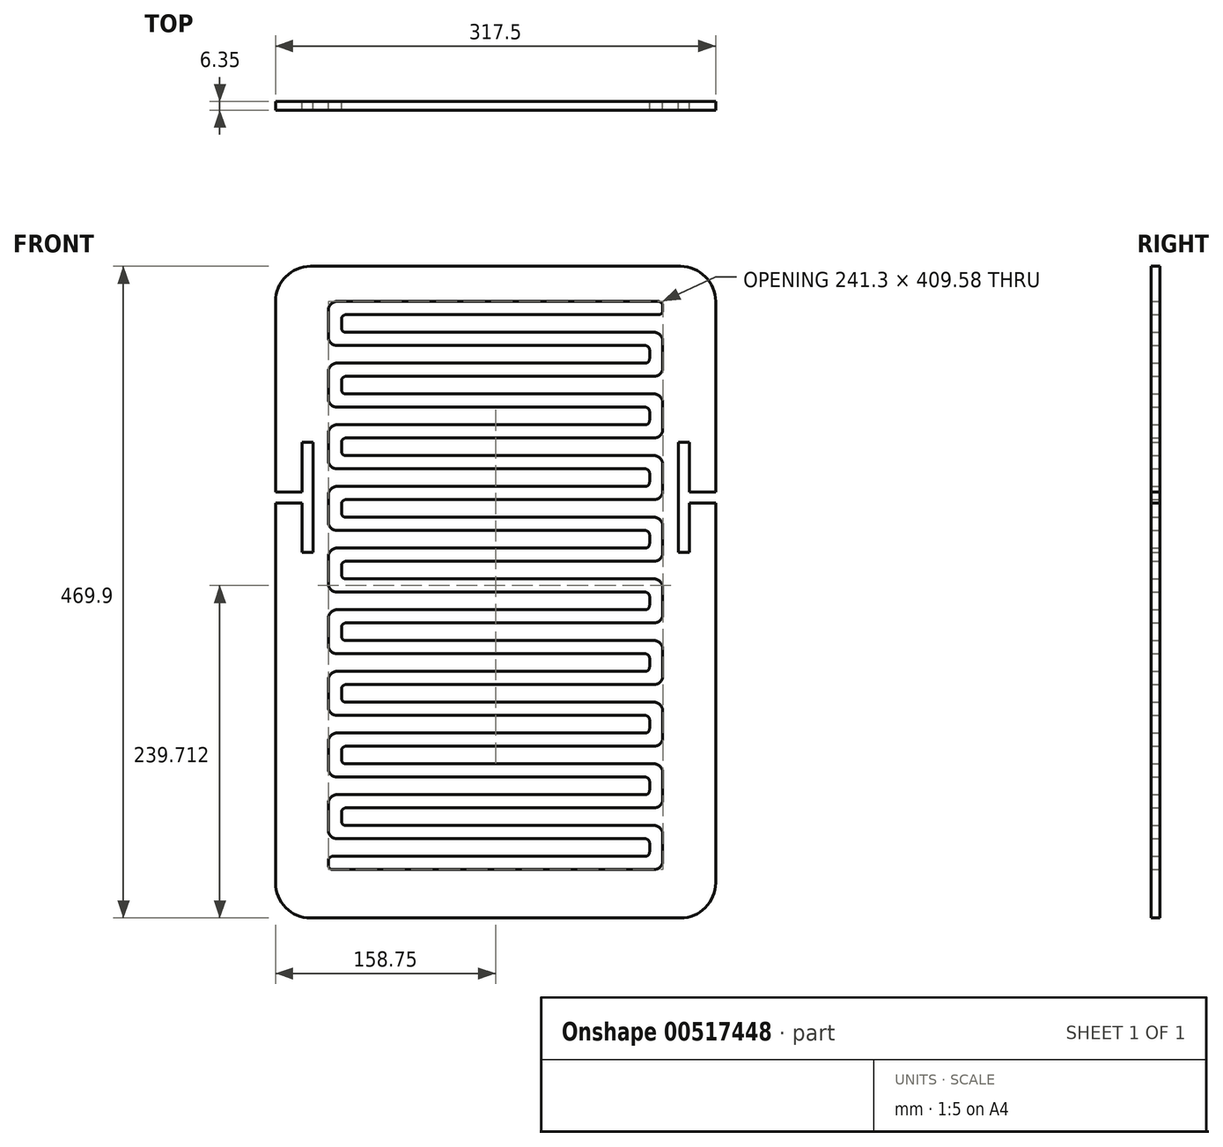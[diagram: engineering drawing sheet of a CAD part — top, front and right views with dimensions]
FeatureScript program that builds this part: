
annotation { "Feature Type Name" : "Feature", "Feature Type Description" : "" }
export const myFeature = defineFeature(function(context is Context, id is Id, definition is map)
    precondition{}
    {
        {
            var Q0;
            Q0=qCreatedBy(makeId("Front.planeOp"),FACE);
            var sketch = newSketch(context, id + "F0", { "sketchPlane" : qUnion([Q0])});
            skLineSegment(sketch, "E0.bottom", {"start": v(133.35, -234.95) * mm, "end": v(-133.35, -234.95) * mm});
            skLineSegment(sketch, "E0.top", {"start": v(133.35, 234.95) * mm, "end": v(-133.35, 234.95) * mm});
            skLineSegment(sketch, "E0.left", {"start": v(158.75, -209.55) * mm, "end": v(158.75, 209.55) * mm});
            skLineSegment(sketch, "E0.right", {"start": v(-158.75, -209.55) * mm, "end": v(-158.75, 209.55) * mm});
            skPoint(sketch, "E0.middle", {"position": v(0, 0) * mm});
            skPoint(sketch, "E1.visualSharp", {"position": v(-158.75, 234.95) * mm});
            skArc(sketch, "E1.filletArc", {"start": v(-133.35, 234.95) * mm, "mid": v(-151.31, 227.51) * mm, "end": v(-158.75, 209.55) * mm});
            skPoint(sketch, "E2.visualSharp", {"position": v(158.75, 234.95) * mm});
            skArc(sketch, "E2.filletArc", {"start": v(158.75, 209.55) * mm, "mid": v(151.31, 227.51) * mm, "end": v(133.35, 234.95) * mm});
            skPoint(sketch, "E3.visualSharp", {"position": v(158.75, -234.95) * mm});
            skArc(sketch, "E3.filletArc", {"start": v(133.35, -234.95) * mm, "mid": v(151.31, -227.51) * mm, "end": v(158.75, -209.55) * mm});
            skPoint(sketch, "E4.visualSharp", {"position": v(-158.75, -234.95) * mm});
            skArc(sketch, "E4.filletArc", {"start": v(-158.75, -209.55) * mm, "mid": v(-151.31, -227.51) * mm, "end": v(-133.35, -234.95) * mm});
            skLineSegment(sketch, "E5.bottom", {"start": v(-139.7, 107.95) * mm, "end": v(-131.76, 107.95) * mm});
            skLineSegment(sketch, "E5.top", {"start": v(-139.7, 28.58) * mm, "end": v(-131.76, 28.58) * mm});
            skLineSegment(sketch, "E5.left", {"start": v(-139.7, 107.95) * mm, "end": v(-139.7, 28.58) * mm});
            skLineSegment(sketch, "E5.right", {"start": v(-131.76, 107.95) * mm, "end": v(-131.76, 28.58) * mm});
            skLineSegment(sketch, "E6.MirrorCS", {"start": v(139.7, 107.95) * mm, "end": v(131.76, 107.95) * mm});
            skLineSegment(sketch, "E7.MirrorCS", {"start": v(139.7, 28.58) * mm, "end": v(131.76, 28.58) * mm});
            skLineSegment(sketch, "E8.MirrorCS", {"start": v(131.76, 107.95) * mm, "end": v(131.76, 28.58) * mm});
            skLineSegment(sketch, "E9.MirrorCS", {"start": v(139.7, 107.95) * mm, "end": v(139.7, 28.58) * mm});
            skLineSegment(sketch, "E10", {"start": v(-114.3, 209.55) * mm, "end": v(117.47, 209.55) * mm});
            skLineSegment(sketch, "E11", {"start": v(120.65, 206.38) * mm, "end": v(120.65, 203.2) * mm});
            skLineSegment(sketch, "E12", {"start": v(117.47, 200.03) * mm, "end": v(-107.95, 200.03) * mm});
            skLineSegment(sketch, "E13", {"start": v(-111.13, 196.85) * mm, "end": v(-111.13, 190.5) * mm});
            skLineSegment(sketch, "E14", {"start": v(-107.95, 187.33) * mm, "end": v(114.3, 187.33) * mm});
            skLineSegment(sketch, "E15", {"start": v(120.65, 180.97) * mm, "end": v(120.65, 161.93) * mm});
            skLineSegment(sketch, "E16", {"start": v(-120.65, 203.2) * mm, "end": v(-120.65, 184.15) * mm});
            skLineSegment(sketch, "E17", {"start": v(-114.3, 177.8) * mm, "end": v(107.95, 177.8) * mm});
            skLineSegment(sketch, "E18", {"start": v(111.12, 174.62) * mm, "end": v(111.12, 168.28) * mm});
            skLineSegment(sketch, "E19", {"start": v(107.95, 165.1) * mm, "end": v(-114.3, 165.1) * mm});
            skPoint(sketch, "E20.visualSharp", {"position": v(-120.65, 209.55) * mm});
            skArc(sketch, "E20.filletArc", {"start": v(-114.3, 209.55) * mm, "mid": v(-118.8, 207.7) * mm, "end": v(-120.65, 203.2) * mm});
            skPoint(sketch, "E21.visualSharp", {"position": v(-111.13, 200.03) * mm});
            skArc(sketch, "E21.filletArc", {"start": v(-107.95, 200.03) * mm, "mid": v(-110.2, 199.1) * mm, "end": v(-111.13, 196.85) * mm});
            skPoint(sketch, "E22.visualSharp", {"position": v(-111.13, 187.33) * mm});
            skArc(sketch, "E22.filletArc", {"start": v(-111.13, 190.5) * mm, "mid": v(-110.2, 188.25) * mm, "end": v(-107.95, 187.33) * mm});
            skPoint(sketch, "E23.visualSharp", {"position": v(-120.65, 177.8) * mm});
            skArc(sketch, "E23.filletArc", {"start": v(-120.65, 184.15) * mm, "mid": v(-118.8, 179.66) * mm, "end": v(-114.3, 177.8) * mm});
            skPoint(sketch, "E24.visualSharp", {"position": v(120.65, 187.33) * mm});
            skArc(sketch, "E24.filletArc", {"start": v(120.65, 180.97) * mm, "mid": v(118.8, 185.47) * mm, "end": v(114.3, 187.32) * mm});
            skPoint(sketch, "E25.visualSharp", {"position": v(120.65, 200.03) * mm});
            skArc(sketch, "E25.filletArc", {"start": v(117.47, 200.03) * mm, "mid": v(119.72, 200.95) * mm, "end": v(120.65, 203.2) * mm});
            skPoint(sketch, "E26.visualSharp", {"position": v(120.65, 209.55) * mm});
            skArc(sketch, "E26.filletArc", {"start": v(120.65, 206.38) * mm, "mid": v(119.72, 208.62) * mm, "end": v(117.47, 209.55) * mm});
            skPoint(sketch, "E27.visualSharp", {"position": v(111.12, 177.8) * mm});
            skArc(sketch, "E27.filletArc", {"start": v(111.12, 174.62) * mm, "mid": v(110.2, 176.87) * mm, "end": v(107.95, 177.8) * mm});
            skPoint(sketch, "E28.visualSharp", {"position": v(111.12, 165.1) * mm});
            skArc(sketch, "E28.filletArc", {"start": v(107.95, 165.1) * mm, "mid": v(110.2, 166.03) * mm, "end": v(111.12, 168.28) * mm});
            skArc(sketch, "E29.filletArc", {"start": v(114.3, 155.58) * mm, "mid": v(118.8, 157.43) * mm, "end": v(120.65, 161.93) * mm});
            skPoint(sketch, "E30.visualSharp", {"position": v(-120.65, 165.1) * mm});
            skLineSegment(sketch, "E31", {"start": v(114.3, 155.58) * mm, "end": v(-107.95, 155.58) * mm});
            skLineSegment(sketch, "E32.0.1.0", {"start": v(114.3, 111.13) * mm, "end": v(-107.95, 111.13) * mm});
            skLineSegment(sketch, "E32.0.1.1", {"start": v(107.95, 120.65) * mm, "end": v(-114.3, 120.65) * mm});
            skArc(sketch, "E32.0.1.2", {"start": v(114.3, 111.13) * mm, "mid": v(118.8, 112.98) * mm, "end": v(120.65, 117.48) * mm});
            skLineSegment(sketch, "E32.0.1.3", {"start": v(120.65, 136.53) * mm, "end": v(120.65, 117.48) * mm});
            skArc(sketch, "E32.0.1.4", {"start": v(107.95, 120.65) * mm, "mid": v(110.2, 121.58) * mm, "end": v(111.12, 123.83) * mm});
            skLineSegment(sketch, "E32.0.1.5", {"start": v(111.13, 130.18) * mm, "end": v(111.13, 123.83) * mm});
            skArc(sketch, "E32.0.1.6", {"start": v(111.12, 130.18) * mm, "mid": v(110.2, 132.42) * mm, "end": v(107.95, 133.35) * mm});
            skArc(sketch, "E32.0.1.7", {"start": v(120.65, 136.53) * mm, "mid": v(118.8, 141.02) * mm, "end": v(114.3, 142.88) * mm});
            skLineSegment(sketch, "E32.0.1.8", {"start": v(-107.95, 142.88) * mm, "end": v(114.3, 142.88) * mm});
            skLineSegment(sketch, "E32.0.1.9", {"start": v(-114.3, 133.35) * mm, "end": v(107.95, 133.35) * mm});
            skArc(sketch, "E32.0.1.10", {"start": v(-120.65, 139.7) * mm, "mid": v(-118.8, 135.2) * mm, "end": v(-114.3, 133.35) * mm});
            skLineSegment(sketch, "E32.0.1.11", {"start": v(-120.65, 158.75) * mm, "end": v(-120.65, 139.7) * mm});
            skArc(sketch, "E32.0.1.12", {"start": v(-114.3, 165.1) * mm, "mid": v(-118.8, 163.24) * mm, "end": v(-120.65, 158.75) * mm});
            skArc(sketch, "E32.0.1.13", {"start": v(-107.95, 155.58) * mm, "mid": v(-110.2, 154.65) * mm, "end": v(-111.13, 152.4) * mm});
            skLineSegment(sketch, "E32.0.1.14", {"start": v(-111.12, 152.4) * mm, "end": v(-111.12, 146.05) * mm});
            skArc(sketch, "E32.0.1.15", {"start": v(-111.13, 146.05) * mm, "mid": v(-110.2, 143.8) * mm, "end": v(-107.95, 142.88) * mm});
            skLineSegment(sketch, "E32.direction1", {"start": v(-107.95, 155.58) * mm, "end": v(-82.55, 155.58) * mm, "construction": true});
            skLineSegment(sketch, "E32.direction2", {"start": v(-107.95, 155.58) * mm, "end": v(-107.95, 111.13) * mm, "construction": true});
            skLineSegment(sketch, "E33.0.0.2", {"start": v(114.3, 66.68) * mm, "end": v(-107.95, 66.68) * mm});
            skLineSegment(sketch, "E33.3.0.2", {"start": v(107.95, 76.2) * mm, "end": v(-114.3, 76.2) * mm});
            skArc(sketch, "E33.6.0.2", {"start": v(114.3, 66.68) * mm, "mid": v(118.8, 68.53) * mm, "end": v(120.65, 73.03) * mm});
            skLineSegment(sketch, "E33.10.0.2", {"start": v(120.65, 92.08) * mm, "end": v(120.65, 73.03) * mm});
            skArc(sketch, "E33.13.0.2", {"start": v(107.95, 76.2) * mm, "mid": v(110.2, 77.13) * mm, "end": v(111.12, 79.38) * mm});
            skLineSegment(sketch, "E33.17.0.2", {"start": v(111.13, 85.73) * mm, "end": v(111.13, 79.38) * mm});
            skArc(sketch, "E33.20.0.2", {"start": v(111.12, 85.73) * mm, "mid": v(110.2, 87.97) * mm, "end": v(107.95, 88.9) * mm});
            skArc(sketch, "E33.24.0.2", {"start": v(120.65, 92.08) * mm, "mid": v(118.8, 96.57) * mm, "end": v(114.3, 98.43) * mm});
            skLineSegment(sketch, "E33.28.0.2", {"start": v(-107.95, 98.43) * mm, "end": v(114.3, 98.43) * mm});
            skLineSegment(sketch, "E33.31.0.2", {"start": v(-114.3, 88.9) * mm, "end": v(107.95, 88.9) * mm});
            skArc(sketch, "E33.34.0.2", {"start": v(-120.65, 95.25) * mm, "mid": v(-118.8, 90.76) * mm, "end": v(-114.3, 88.9) * mm});
            skLineSegment(sketch, "E33.38.0.2", {"start": v(-120.65, 114.3) * mm, "end": v(-120.65, 95.25) * mm});
            skArc(sketch, "E33.41.0.2", {"start": v(-114.3, 120.65) * mm, "mid": v(-118.8, 118.8) * mm, "end": v(-120.65, 114.3) * mm});
            skArc(sketch, "E33.45.0.2", {"start": v(-107.95, 111.13) * mm, "mid": v(-110.2, 110.2) * mm, "end": v(-111.13, 107.95) * mm});
            skLineSegment(sketch, "E33.49.0.2", {"start": v(-111.12, 107.95) * mm, "end": v(-111.12, 101.6) * mm});
            skArc(sketch, "E33.52.0.2", {"start": v(-111.13, 101.6) * mm, "mid": v(-110.2, 99.35) * mm, "end": v(-107.95, 98.43) * mm});
            skLineSegment(sketch, "E33.0.0.3", {"start": v(114.3, 22.23) * mm, "end": v(-107.95, 22.23) * mm});
            skLineSegment(sketch, "E33.3.0.3", {"start": v(107.95, 31.75) * mm, "end": v(-114.3, 31.75) * mm});
            skArc(sketch, "E33.6.0.3", {"start": v(114.3, 22.23) * mm, "mid": v(118.8, 24.08) * mm, "end": v(120.65, 28.58) * mm});
            skLineSegment(sketch, "E33.10.0.3", {"start": v(120.65, 47.63) * mm, "end": v(120.65, 28.58) * mm});
            skArc(sketch, "E33.13.0.3", {"start": v(107.95, 31.75) * mm, "mid": v(110.2, 32.68) * mm, "end": v(111.12, 34.93) * mm});
            skLineSegment(sketch, "E33.17.0.3", {"start": v(111.13, 41.28) * mm, "end": v(111.13, 34.93) * mm});
            skArc(sketch, "E33.20.0.3", {"start": v(111.12, 41.28) * mm, "mid": v(110.2, 43.52) * mm, "end": v(107.95, 44.45) * mm});
            skArc(sketch, "E33.24.0.3", {"start": v(120.65, 47.63) * mm, "mid": v(118.8, 52.12) * mm, "end": v(114.3, 53.98) * mm});
            skLineSegment(sketch, "E33.28.0.3", {"start": v(-107.95, 53.98) * mm, "end": v(114.3, 53.98) * mm});
            skLineSegment(sketch, "E33.31.0.3", {"start": v(-114.3, 44.45) * mm, "end": v(107.95, 44.45) * mm});
            skArc(sketch, "E33.34.0.3", {"start": v(-120.65, 50.8) * mm, "mid": v(-118.8, 46.3) * mm, "end": v(-114.3, 44.45) * mm});
            skLineSegment(sketch, "E33.38.0.3", {"start": v(-120.65, 69.85) * mm, "end": v(-120.65, 50.8) * mm});
            skArc(sketch, "E33.41.0.3", {"start": v(-114.3, 76.2) * mm, "mid": v(-118.8, 74.34) * mm, "end": v(-120.65, 69.85) * mm});
            skArc(sketch, "E33.45.0.3", {"start": v(-107.95, 66.68) * mm, "mid": v(-110.2, 65.75) * mm, "end": v(-111.13, 63.5) * mm});
            skLineSegment(sketch, "E33.49.0.3", {"start": v(-111.12, 63.5) * mm, "end": v(-111.12, 57.15) * mm});
            skArc(sketch, "E33.52.0.3", {"start": v(-111.13, 57.15) * mm, "mid": v(-110.2, 54.9) * mm, "end": v(-107.95, 53.98) * mm});
            skLineSegment(sketch, "E33.0.0.4", {"start": v(114.3, -22.22) * mm, "end": v(-107.95, -22.22) * mm});
            skLineSegment(sketch, "E33.3.0.4", {"start": v(107.95, -12.7) * mm, "end": v(-114.3, -12.7) * mm});
            skArc(sketch, "E33.6.0.4", {"start": v(114.3, -22.22) * mm, "mid": v(118.8, -20.37) * mm, "end": v(120.65, -15.87) * mm});
            skLineSegment(sketch, "E33.10.0.4", {"start": v(120.65, 3.18) * mm, "end": v(120.65, -15.87) * mm});
            skArc(sketch, "E33.13.0.4", {"start": v(107.95, -12.7) * mm, "mid": v(110.2, -11.77) * mm, "end": v(111.12, -9.52) * mm});
            skLineSegment(sketch, "E33.17.0.4", {"start": v(111.13, -3.17) * mm, "end": v(111.13, -9.52) * mm});
            skArc(sketch, "E33.20.0.4", {"start": v(111.12, -3.17) * mm, "mid": v(110.2, -0.93) * mm, "end": v(107.95, 0) * mm});
            skArc(sketch, "E33.24.0.4", {"start": v(120.65, 3.18) * mm, "mid": v(118.8, 7.67) * mm, "end": v(114.3, 9.53) * mm});
            skLineSegment(sketch, "E33.28.0.4", {"start": v(-107.95, 9.53) * mm, "end": v(114.3, 9.53) * mm});
            skLineSegment(sketch, "E33.31.0.4", {"start": v(-114.3, 0) * mm, "end": v(107.95, 0) * mm});
            skArc(sketch, "E33.34.0.4", {"start": v(-120.65, 6.35) * mm, "mid": v(-118.8, 1.86) * mm, "end": v(-114.3, 0) * mm});
            skLineSegment(sketch, "E33.38.0.4", {"start": v(-120.65, 25.4) * mm, "end": v(-120.65, 6.35) * mm});
            skArc(sketch, "E33.41.0.4", {"start": v(-114.3, 31.75) * mm, "mid": v(-118.8, 29.9) * mm, "end": v(-120.65, 25.4) * mm});
            skArc(sketch, "E33.45.0.4", {"start": v(-107.95, 22.23) * mm, "mid": v(-110.2, 21.3) * mm, "end": v(-111.13, 19.05) * mm});
            skLineSegment(sketch, "E33.49.0.4", {"start": v(-111.12, 19.05) * mm, "end": v(-111.12, 12.7) * mm});
            skArc(sketch, "E33.52.0.4", {"start": v(-111.13, 12.7) * mm, "mid": v(-110.2, 10.45) * mm, "end": v(-107.95, 9.53) * mm});
            skLineSegment(sketch, "E33.0.0.5", {"start": v(114.3, -66.67) * mm, "end": v(-107.95, -66.67) * mm});
            skLineSegment(sketch, "E33.3.0.5", {"start": v(107.95, -57.15) * mm, "end": v(-114.3, -57.15) * mm});
            skArc(sketch, "E33.6.0.5", {"start": v(114.3, -66.67) * mm, "mid": v(118.8, -64.82) * mm, "end": v(120.65, -60.32) * mm});
            skLineSegment(sketch, "E33.10.0.5", {"start": v(120.65, -41.27) * mm, "end": v(120.65, -60.32) * mm});
            skArc(sketch, "E33.13.0.5", {"start": v(107.95, -57.15) * mm, "mid": v(110.2, -56.22) * mm, "end": v(111.12, -53.97) * mm});
            skLineSegment(sketch, "E33.17.0.5", {"start": v(111.13, -47.62) * mm, "end": v(111.13, -53.97) * mm});
            skArc(sketch, "E33.20.0.5", {"start": v(111.12, -47.62) * mm, "mid": v(110.2, -45.38) * mm, "end": v(107.95, -44.45) * mm});
            skArc(sketch, "E33.24.0.5", {"start": v(120.65, -41.27) * mm, "mid": v(118.8, -36.78) * mm, "end": v(114.3, -34.92) * mm});
            skLineSegment(sketch, "E33.28.0.5", {"start": v(-107.95, -34.92) * mm, "end": v(114.3, -34.92) * mm});
            skLineSegment(sketch, "E33.31.0.5", {"start": v(-114.3, -44.45) * mm, "end": v(107.95, -44.45) * mm});
            skArc(sketch, "E33.34.0.5", {"start": v(-120.65, -38.1) * mm, "mid": v(-118.8, -42.6) * mm, "end": v(-114.3, -44.45) * mm});
            skLineSegment(sketch, "E33.38.0.5", {"start": v(-120.65, -19.05) * mm, "end": v(-120.65, -38.1) * mm});
            skArc(sketch, "E33.41.0.5", {"start": v(-114.3, -12.7) * mm, "mid": v(-118.8, -14.56) * mm, "end": v(-120.65, -19.05) * mm});
            skArc(sketch, "E33.45.0.5", {"start": v(-107.95, -22.22) * mm, "mid": v(-110.2, -23.15) * mm, "end": v(-111.13, -25.4) * mm});
            skLineSegment(sketch, "E33.49.0.5", {"start": v(-111.12, -25.4) * mm, "end": v(-111.12, -31.75) * mm});
            skArc(sketch, "E33.52.0.5", {"start": v(-111.13, -31.75) * mm, "mid": v(-110.2, -34) * mm, "end": v(-107.95, -34.92) * mm});
            skLineSegment(sketch, "E33.0.0.6", {"start": v(114.3, -111.12) * mm, "end": v(-107.95, -111.12) * mm});
            skLineSegment(sketch, "E33.3.0.6", {"start": v(107.95, -101.6) * mm, "end": v(-114.3, -101.6) * mm});
            skArc(sketch, "E33.6.0.6", {"start": v(114.3, -111.12) * mm, "mid": v(118.8, -109.27) * mm, "end": v(120.65, -104.77) * mm});
            skLineSegment(sketch, "E33.10.0.6", {"start": v(120.65, -85.72) * mm, "end": v(120.65, -104.77) * mm});
            skArc(sketch, "E33.13.0.6", {"start": v(107.95, -101.6) * mm, "mid": v(110.2, -100.67) * mm, "end": v(111.12, -98.42) * mm});
            skLineSegment(sketch, "E33.17.0.6", {"start": v(111.13, -92.07) * mm, "end": v(111.13, -98.42) * mm});
            skArc(sketch, "E33.20.0.6", {"start": v(111.12, -92.07) * mm, "mid": v(110.2, -89.83) * mm, "end": v(107.95, -88.9) * mm});
            skArc(sketch, "E33.24.0.6", {"start": v(120.65, -85.72) * mm, "mid": v(118.8, -81.23) * mm, "end": v(114.3, -79.37) * mm});
            skLineSegment(sketch, "E33.28.0.6", {"start": v(-107.95, -79.37) * mm, "end": v(114.3, -79.37) * mm});
            skLineSegment(sketch, "E33.31.0.6", {"start": v(-114.3, -88.9) * mm, "end": v(107.95, -88.9) * mm});
            skArc(sketch, "E33.34.0.6", {"start": v(-120.65, -82.55) * mm, "mid": v(-118.8, -87.04) * mm, "end": v(-114.3, -88.9) * mm});
            skLineSegment(sketch, "E33.38.0.6", {"start": v(-120.65, -63.5) * mm, "end": v(-120.65, -82.55) * mm});
            skArc(sketch, "E33.41.0.6", {"start": v(-114.3, -57.15) * mm, "mid": v(-118.8, -59) * mm, "end": v(-120.65, -63.5) * mm});
            skArc(sketch, "E33.45.0.6", {"start": v(-107.95, -66.67) * mm, "mid": v(-110.2, -67.6) * mm, "end": v(-111.13, -69.85) * mm});
            skLineSegment(sketch, "E33.49.0.6", {"start": v(-111.12, -69.85) * mm, "end": v(-111.12, -76.2) * mm});
            skArc(sketch, "E33.52.0.6", {"start": v(-111.13, -76.2) * mm, "mid": v(-110.2, -78.45) * mm, "end": v(-107.95, -79.37) * mm});
            skLineSegment(sketch, "E33.0.0.7", {"start": v(114.3, -155.57) * mm, "end": v(-107.95, -155.57) * mm});
            skLineSegment(sketch, "E33.3.0.7", {"start": v(107.95, -146.05) * mm, "end": v(-114.3, -146.05) * mm});
            skArc(sketch, "E33.6.0.7", {"start": v(114.3, -155.57) * mm, "mid": v(118.8, -153.72) * mm, "end": v(120.65, -149.22) * mm});
            skLineSegment(sketch, "E33.10.0.7", {"start": v(120.65, -130.17) * mm, "end": v(120.65, -149.22) * mm});
            skArc(sketch, "E33.13.0.7", {"start": v(107.95, -146.05) * mm, "mid": v(110.2, -145.12) * mm, "end": v(111.12, -142.87) * mm});
            skLineSegment(sketch, "E33.17.0.7", {"start": v(111.13, -136.52) * mm, "end": v(111.13, -142.87) * mm});
            skArc(sketch, "E33.20.0.7", {"start": v(111.12, -136.52) * mm, "mid": v(110.2, -134.28) * mm, "end": v(107.95, -133.35) * mm});
            skArc(sketch, "E33.24.0.7", {"start": v(120.65, -130.17) * mm, "mid": v(118.8, -125.68) * mm, "end": v(114.3, -123.82) * mm});
            skLineSegment(sketch, "E33.28.0.7", {"start": v(-107.95, -123.82) * mm, "end": v(114.3, -123.82) * mm});
            skLineSegment(sketch, "E33.31.0.7", {"start": v(-114.3, -133.35) * mm, "end": v(107.95, -133.35) * mm});
            skArc(sketch, "E33.34.0.7", {"start": v(-120.65, -127) * mm, "mid": v(-118.8, -131.5) * mm, "end": v(-114.3, -133.35) * mm});
            skLineSegment(sketch, "E33.38.0.7", {"start": v(-120.65, -107.95) * mm, "end": v(-120.65, -127) * mm});
            skArc(sketch, "E33.41.0.7", {"start": v(-114.3, -101.6) * mm, "mid": v(-118.8, -103.46) * mm, "end": v(-120.65, -107.95) * mm});
            skArc(sketch, "E33.45.0.7", {"start": v(-107.95, -111.12) * mm, "mid": v(-110.2, -112.05) * mm, "end": v(-111.13, -114.3) * mm});
            skLineSegment(sketch, "E33.49.0.7", {"start": v(-111.12, -114.3) * mm, "end": v(-111.12, -120.65) * mm});
            skArc(sketch, "E33.52.0.7", {"start": v(-111.13, -120.65) * mm, "mid": v(-110.2, -122.9) * mm, "end": v(-107.95, -123.82) * mm});
            skPoint(sketch, "E34.visualSharp", {"position": v(120.65, -352.42) * mm});
            skArc(sketch, "E34.filletArc", {"start": v(120.65, -355.6) * mm, "mid": v(119.72, -353.35) * mm, "end": v(117.47, -352.42) * mm});
            skPoint(sketch, "E35.visualSharp", {"position": v(120.65, -361.95) * mm});
            skArc(sketch, "E35.filletArc", {"start": v(117.47, -361.95) * mm, "mid": v(119.72, -361.02) * mm, "end": v(120.65, -358.77) * mm});
            skLineSegment(sketch, "E36", {"start": v(-139.7, 68.26) * mm, "end": v(-158.75, 68.26) * mm, "construction": true});
            skLineSegment(sketch, "E37.bottom", {"start": v(-158.75, 72.23) * mm, "end": v(-139.7, 72.23) * mm});
            skLineSegment(sketch, "E37.top", {"start": v(-158.75, 64.3) * mm, "end": v(-139.7, 64.3) * mm});
            skLineSegment(sketch, "E37.left", {"start": v(-158.75, 72.23) * mm, "end": v(-158.75, 64.3) * mm});
            skLineSegment(sketch, "E37.right", {"start": v(-139.7, 72.23) * mm, "end": v(-139.7, 64.3) * mm});
            skLineSegment(sketch, "E38.MirrorCS", {"start": v(-139.7, 64.3) * mm, "end": v(-139.7, 72.23) * mm});
            skLineSegment(sketch, "E39.MirrorCS", {"start": v(-158.75, 64.3) * mm, "end": v(-158.75, 72.23) * mm});
            skLineSegment(sketch, "E40.MirrorCS", {"start": v(158.75, 72.23) * mm, "end": v(158.75, 64.3) * mm});
            skLineSegment(sketch, "E41.MirrorCS", {"start": v(139.7, 72.23) * mm, "end": v(139.7, 64.3) * mm});
            skLineSegment(sketch, "E42.MirrorCS", {"start": v(158.75, 72.23) * mm, "end": v(139.7, 72.23) * mm});
            skLineSegment(sketch, "E43.MirrorCS", {"start": v(158.75, 64.3) * mm, "end": v(139.7, 64.3) * mm});
            skLineSegment(sketch, "E44.MirrorCS", {"start": v(139.7, 64.3) * mm, "end": v(139.7, 72.23) * mm});
            skLineSegment(sketch, "E45.MirrorCS", {"start": v(158.75, 64.3) * mm, "end": v(158.75, 72.23) * mm});
            skLineSegment(sketch, "E46.MirrorCS", {"start": v(139.7, 68.26) * mm, "end": v(158.75, 68.26) * mm, "construction": true});
            skLineSegment(sketch, "E47.0.0.8", {"start": v(114.3, -200.02) * mm, "end": v(-107.95, -200.02) * mm});
            skLineSegment(sketch, "E47.3.0.8", {"start": v(107.95, -190.5) * mm, "end": v(-114.3, -190.5) * mm});
            skArc(sketch, "E47.6.0.8", {"start": v(114.3, -200.02) * mm, "mid": v(118.8, -198.17) * mm, "end": v(120.65, -193.67) * mm});
            skLineSegment(sketch, "E47.10.0.8", {"start": v(120.65, -174.62) * mm, "end": v(120.65, -193.67) * mm});
            skArc(sketch, "E47.13.0.8", {"start": v(107.95, -190.5) * mm, "mid": v(110.2, -189.57) * mm, "end": v(111.12, -187.32) * mm});
            skLineSegment(sketch, "E47.17.0.8", {"start": v(111.12, -180.97) * mm, "end": v(111.12, -187.32) * mm});
            skArc(sketch, "E47.20.0.8", {"start": v(111.12, -180.97) * mm, "mid": v(110.2, -178.73) * mm, "end": v(107.95, -177.8) * mm});
            skArc(sketch, "E47.24.0.8", {"start": v(120.65, -174.62) * mm, "mid": v(118.8, -170.13) * mm, "end": v(114.3, -168.27) * mm});
            skLineSegment(sketch, "E47.28.0.8", {"start": v(-107.95, -168.27) * mm, "end": v(114.3, -168.27) * mm});
            skLineSegment(sketch, "E47.31.0.8", {"start": v(-114.3, -177.8) * mm, "end": v(107.95, -177.8) * mm});
            skArc(sketch, "E47.34.0.8", {"start": v(-120.65, -171.45) * mm, "mid": v(-118.8, -175.94) * mm, "end": v(-114.3, -177.8) * mm});
            skLineSegment(sketch, "E47.38.0.8", {"start": v(-120.65, -152.4) * mm, "end": v(-120.65, -171.45) * mm});
            skArc(sketch, "E47.41.0.8", {"start": v(-114.3, -146.05) * mm, "mid": v(-118.8, -147.9) * mm, "end": v(-120.65, -152.4) * mm});
            skArc(sketch, "E47.45.0.8", {"start": v(-107.95, -155.57) * mm, "mid": v(-110.2, -156.5) * mm, "end": v(-111.13, -158.75) * mm});
            skLineSegment(sketch, "E47.49.0.8", {"start": v(-111.13, -158.75) * mm, "end": v(-111.13, -165.1) * mm});
            skArc(sketch, "E47.52.0.8", {"start": v(-111.13, -165.1) * mm, "mid": v(-110.2, -167.35) * mm, "end": v(-107.95, -168.27) * mm});
            skLineSegment(sketch, "E48", {"start": v(-107.95, -200.02) * mm, "end": v(-117.48, -200.02) * mm});
            skLineSegment(sketch, "E49", {"start": v(-114.3, -190.5) * mm, "end": v(-117.48, -190.5) * mm});
            skLineSegment(sketch, "E50", {"start": v(-120.65, -193.67) * mm, "end": v(-120.65, -196.85) * mm});
            skPoint(sketch, "E51.visualSharp", {"position": v(-120.65, -190.5) * mm});
            skArc(sketch, "E51.filletArc", {"start": v(-117.48, -190.5) * mm, "mid": v(-119.72, -191.43) * mm, "end": v(-120.65, -193.67) * mm});
            skPoint(sketch, "E52.visualSharp", {"position": v(-120.65, -200.02) * mm});
            skArc(sketch, "E52.filletArc", {"start": v(-120.65, -196.85) * mm, "mid": v(-119.72, -199.1) * mm, "end": v(-117.48, -200.02) * mm});
            skSolve(sketch);
        }
        {
            var Q0;
            Q0=makeQuery(id+"F0.imprint","IMPRINT",FACE,{"disambiguationData":[TD([[makeQuery(id+"F0.imprint","IMPRINT",EDGE,{"derivedFrom":sQuery(id+"F0.wireOp",EDGE,"E0.bottom")}),-1.0]])]});
            extrude(context, id + "F1", {"entities" : qUnion([Q0]), "depth" : 6.35 * mm, "offsetDistance" : 25.4 * mm});
        }
    });
